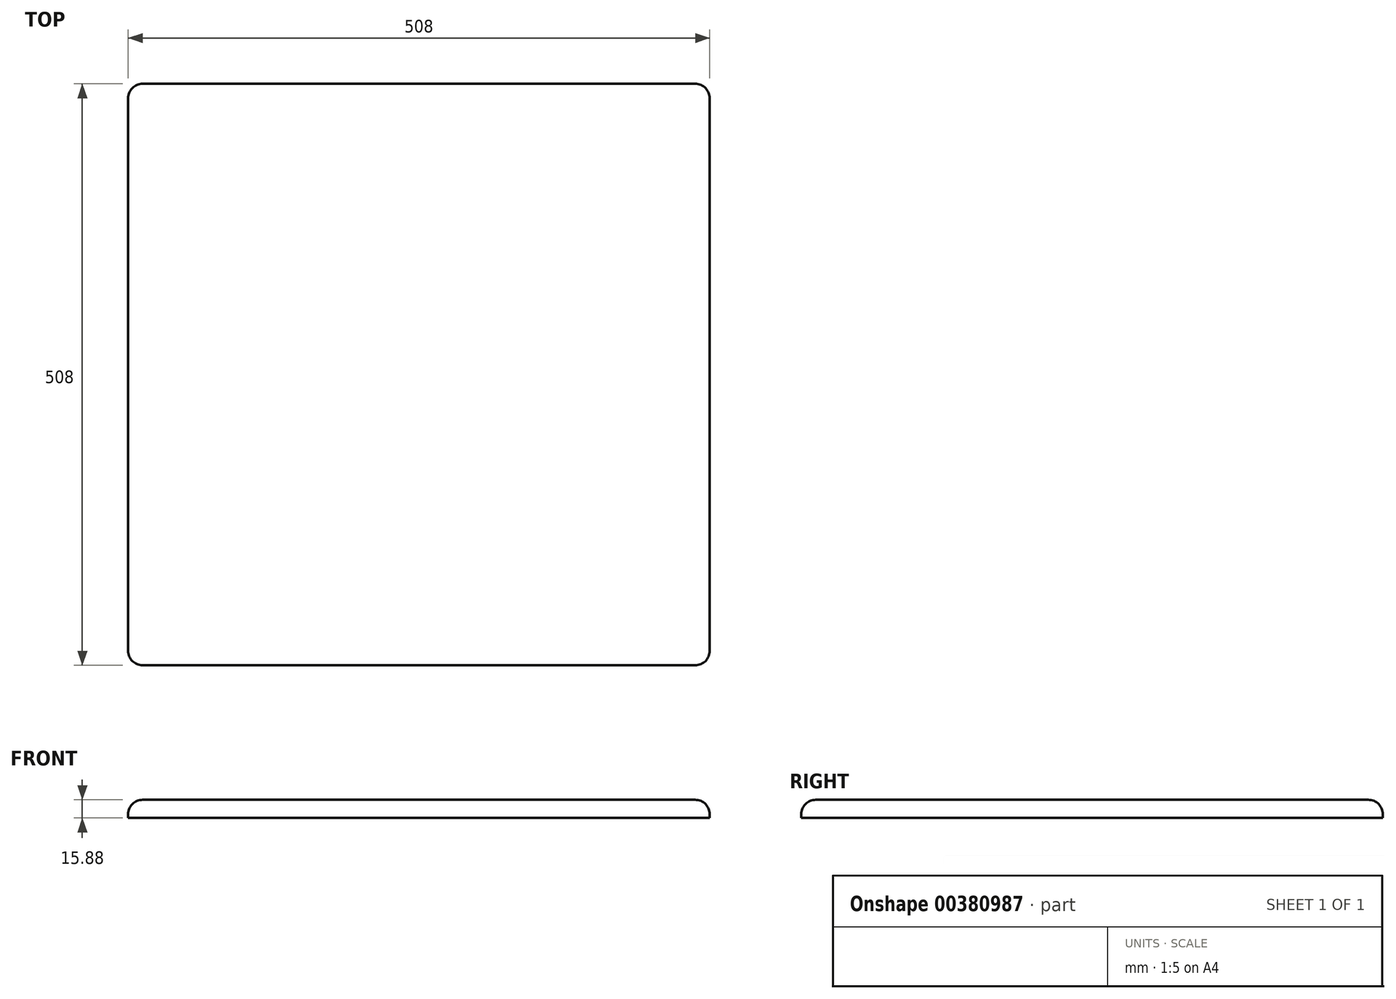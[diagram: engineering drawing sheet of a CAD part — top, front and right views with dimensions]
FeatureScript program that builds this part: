
annotation { "Feature Type Name" : "Feature", "Feature Type Description" : "" }
export const myFeature = defineFeature(function(context is Context, id is Id, definition is map)
    precondition{}
    {
        {
            var Q0;
            Q0=qCreatedBy(makeId("Top.planeOp"),FACE);
            var sketch = newSketch(context, id + "F0", { "sketchPlane" : qUnion([Q0])});
            skLineSegment(sketch, "E0", {"start": v(-255.66, 243.1) * mm, "end": v(-255.66, -264.9) * mm});
            skLineSegment(sketch, "E1", {"start": v(-255.66, -264.9) * mm, "end": v(252.34, -264.9) * mm});
            skLineSegment(sketch, "E2", {"start": v(252.34, -264.9) * mm, "end": v(252.34, 243.1) * mm});
            skLineSegment(sketch, "E3", {"start": v(252.34, 243.1) * mm, "end": v(-255.66, 243.1) * mm});
            skSolve(sketch);
        }
        {
            var Q0;
            Q0=makeQuery(id+"F0.imprint","IMPRINT",FACE,{"disambiguationData":[TD([[makeQuery(id+"F0.imprint","IMPRINT",EDGE,{"derivedFrom":sQuery(id+"F0.wireOp",EDGE,"E0")}),1.0]])]});
            extrude(context, id + "F1", {"entities" : qUnion([Q0]), "depth" : 15.88 * mm});
        }
        {
            var Q0;
            Q0=makeQuery(id+"F1.opExtrude","CAP_FACE",FACE,{"disambiguationData":[OSD([sQuery(id+"F0.wireOp",EDGE,"E0"),sQuery(id+"F0.wireOp",EDGE,"E1"),sQuery(id+"F0.wireOp",EDGE,"E2"),sQuery(id+"F0.wireOp",EDGE,"E3")])],"isStart":false});
            var sketch = newSketch(context, id + "F2", { "sketchPlane" : qUnion([Q0])});
            skCircle(sketch, "E4", {"center": v(0, 0) * mm, "radius": 44.45 * mm});
            skSolve(sketch);
        }
        {
            var Q0;
            Q0=sQuery(id+"F2.wireOp",EDGE,"E4");
            extrude(context, id + "F3", {"bodyType" : ToolBodyType.SURFACE, "surfaceEntities" : qUnion([Q0]), "depth" : 381 * mm});
        }
        {
            var Q0;
            Q0=makeQuery(id+"F1.opExtrude","SWEPT_EDGE",EDGE,{"disambiguationData":[OSD([sQuery(id+"F0.wireOp",EDGE,"E2"),sQuery(id+"F0.wireOp",EDGE,"E3")])]});
            var Q1;
            Q1=makeQuery(id+"F1.opExtrude","SWEPT_EDGE",EDGE,{"disambiguationData":[OSD([sQuery(id+"F0.wireOp",EDGE,"E1"),sQuery(id+"F0.wireOp",EDGE,"E2")])]});
            fillet(context, id + "F4", {"entities" : qUnion([Q0, Q1]), "radius" : 12.7 * mm, "tangentPropagation" : true, "allowEdgeOverflow" : false});
        }
        {
            var Q0;
            Q0=makeQuery(id+"F1.opExtrude","SWEPT_EDGE",EDGE,{"disambiguationData":[OSD([sQuery(id+"F0.wireOp",EDGE,"E0"),sQuery(id+"F0.wireOp",EDGE,"E3")])]});
            var Q1;
            Q1=makeQuery(id+"F1.opExtrude","SWEPT_EDGE",EDGE,{"disambiguationData":[OSD([sQuery(id+"F0.wireOp",EDGE,"E0"),sQuery(id+"F0.wireOp",EDGE,"E1")])]});
            fillet(context, id + "F5", {"entities" : qUnion([Q0, Q1]), "radius" : 12.7 * mm, "tangentPropagation" : true, "allowEdgeOverflow" : false});
        }
        {
            var Q0;
            Q0=makeQuery(id+"F1.opExtrude","CAP_FACE",FACE,{"disambiguationData":[OSD([sQuery(id+"F0.wireOp",EDGE,"E0"),sQuery(id+"F0.wireOp",EDGE,"E1"),sQuery(id+"F0.wireOp",EDGE,"E2"),sQuery(id+"F0.wireOp",EDGE,"E3")])],"isStart":false});
            fillet(context, id + "F6", {"entities" : qUnion([Q0]), "radius" : 12.7 * mm, "tangentPropagation" : true, "allowEdgeOverflow" : false});
        }
    });
